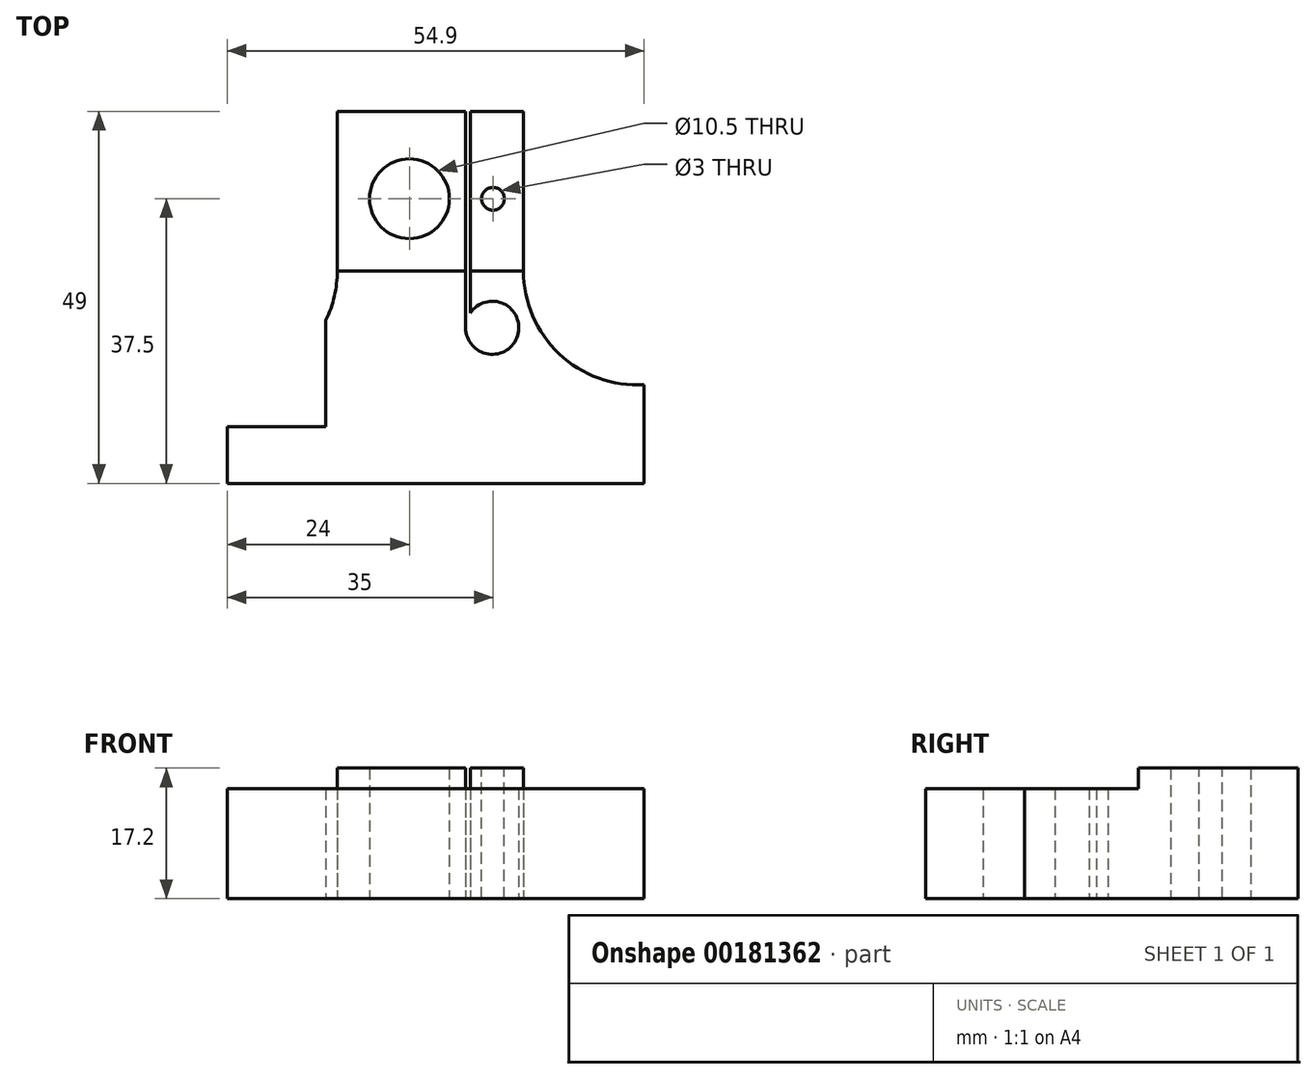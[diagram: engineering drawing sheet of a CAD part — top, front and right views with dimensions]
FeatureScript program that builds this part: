
annotation { "Feature Type Name" : "Feature", "Feature Type Description" : "" }
export const myFeature = defineFeature(function(context is Context, id is Id, definition is map)
    precondition{}
    {
        {
            var Q0;
            Q0=qCreatedBy(makeId("Top.planeOp"),FACE);
            var sketch = newSketch(context, id + "F0", { "sketchPlane" : qUnion([Q0])});
            skCircle(sketch, "E0", {"center": v(0, 0) * mm, "radius": 5.25 * mm});
            skLineSegment(sketch, "E1", {"start": v(-9.5, 11.5) * mm, "end": v(-9.5, -9.5) * mm});
            skLineSegment(sketch, "E2", {"start": v(-11, -16) * mm, "end": v(-11, -30) * mm});
            skLineSegment(sketch, "E3", {"start": v(-9.5, 11.5) * mm, "end": v(7.4, 11.5) * mm});
            skLineSegment(sketch, "E4", {"start": v(-24, -37.5) * mm, "end": v(30.9, -37.5) * mm});
            skLineSegment(sketch, "E5", {"start": v(7.4, 11.5) * mm, "end": v(7.4, -17) * mm});
            skArc(sketch, "E6", {"start": v(7.4, -17) * mm, "mid": v(14.25, -18.02) * mm, "end": v(8, -15.04) * mm});
            skLineSegment(sketch, "E7", {"start": v(8, 11.5) * mm, "end": v(8, -15.04) * mm});
            skLineSegment(sketch, "E8.trimOffspring", {"start": v(8, 11.5) * mm, "end": v(15, 11.5) * mm});
            skLineSegment(sketch, "E9", {"start": v(15, 11.5) * mm, "end": v(15, -9.5) * mm});
            skLineSegment(sketch, "E10", {"start": v(-11, -30) * mm, "end": v(-24, -30) * mm});
            skLineSegment(sketch, "E11", {"start": v(-24, -30) * mm, "end": v(-24, -37.5) * mm});
            skArc(sketch, "E12", {"start": v(15, -9.5) * mm, "mid": v(19.71, -20.43) * mm, "end": v(30.9, -24.5) * mm});
            skLineSegment(sketch, "E13", {"start": v(30.9, -24.5) * mm, "end": v(30.9, -37.5) * mm});
            skLineSegment(sketch, "E14", {"start": v(-9.5, -9.5) * mm, "end": v(7.4, -9.5) * mm});
            skLineSegment(sketch, "E15.trimOffspring", {"start": v(8, -9.5) * mm, "end": v(15, -9.5) * mm});
            skArc(sketch, "E16", {"start": v(-11, -16) * mm, "mid": v(-9.88, -12.84) * mm, "end": v(-9.5, -9.5) * mm});
            skSolve(sketch);
        }
        {
            var Q0;
            Q0=makeQuery(id+"F0.imprint","IMPRINT",FACE,{"disambiguationData":[TD([[makeQuery(id+"F0.imprint","IMPRINT",EDGE,{"derivedFrom":sQuery(id+"F0.wireOp",EDGE,"E2")}),1.0]])]});
            extrude(context, id + "F1", {"entities" : qUnion([Q0]), "depth" : 14.5 * mm});
        }
        {
            var Q0;
            Q0=makeQuery(id+"F0.imprint","IMPRINT",FACE,{"disambiguationData":[TD([[makeQuery(id+"F0.imprint","IMPRINT",EDGE,{"derivedFrom":sQuery(id+"F0.wireOp",EDGE,"E0")}),-1.0]])]});
            var Q1;
            {var subQ0=sQuery(id+"F0.wireOp",EDGE,"E8.trimOffspring");Q1=makeQuery(id+"F0.imprint","IMPRINT",FACE,{"disambiguationData":[TD([[makeQuery(id+"F0.imprint","IMPRINT",EDGE,{"derivedFrom":subQ0}),-1.0]])]});}
            extrude(context, id + "F2", {"entities" : qUnion([Q0, Q1]), "operationType" : NewBodyOperationType.ADD, "depth" : 17.2 * mm});
        }
        {
            var Q0;
            Q0=makeQuery(id+"F2.opExtrude","CAP_FACE",FACE,{"disambiguationData":[OSD([sQuery(id+"F0.wireOp",EDGE,"E7"),sQuery(id+"F0.wireOp",EDGE,"E8.trimOffspring"),sQuery(id+"F0.wireOp",EDGE,"E9"),sQuery(id+"F0.wireOp",EDGE,"E15.trimOffspring")])],"isStart":false});
            var sketch = newSketch(context, id + "F3", { "sketchPlane" : qUnion([Q0])});
            skCircle(sketch, "E17", {"center": v(11, 0) * mm, "radius": 1.5 * mm});
            skSolve(sketch);
        }
        {
            var Q0;
            Q0 = qSketchRegion(id + "F3", true);
            extrude(context, id + "F4", {"entities" : qUnion([Q0]), "operationType" : NewBodyOperationType.REMOVE, "oppositeDirection" : true, "depth" : 25 * mm});
        }
    });
